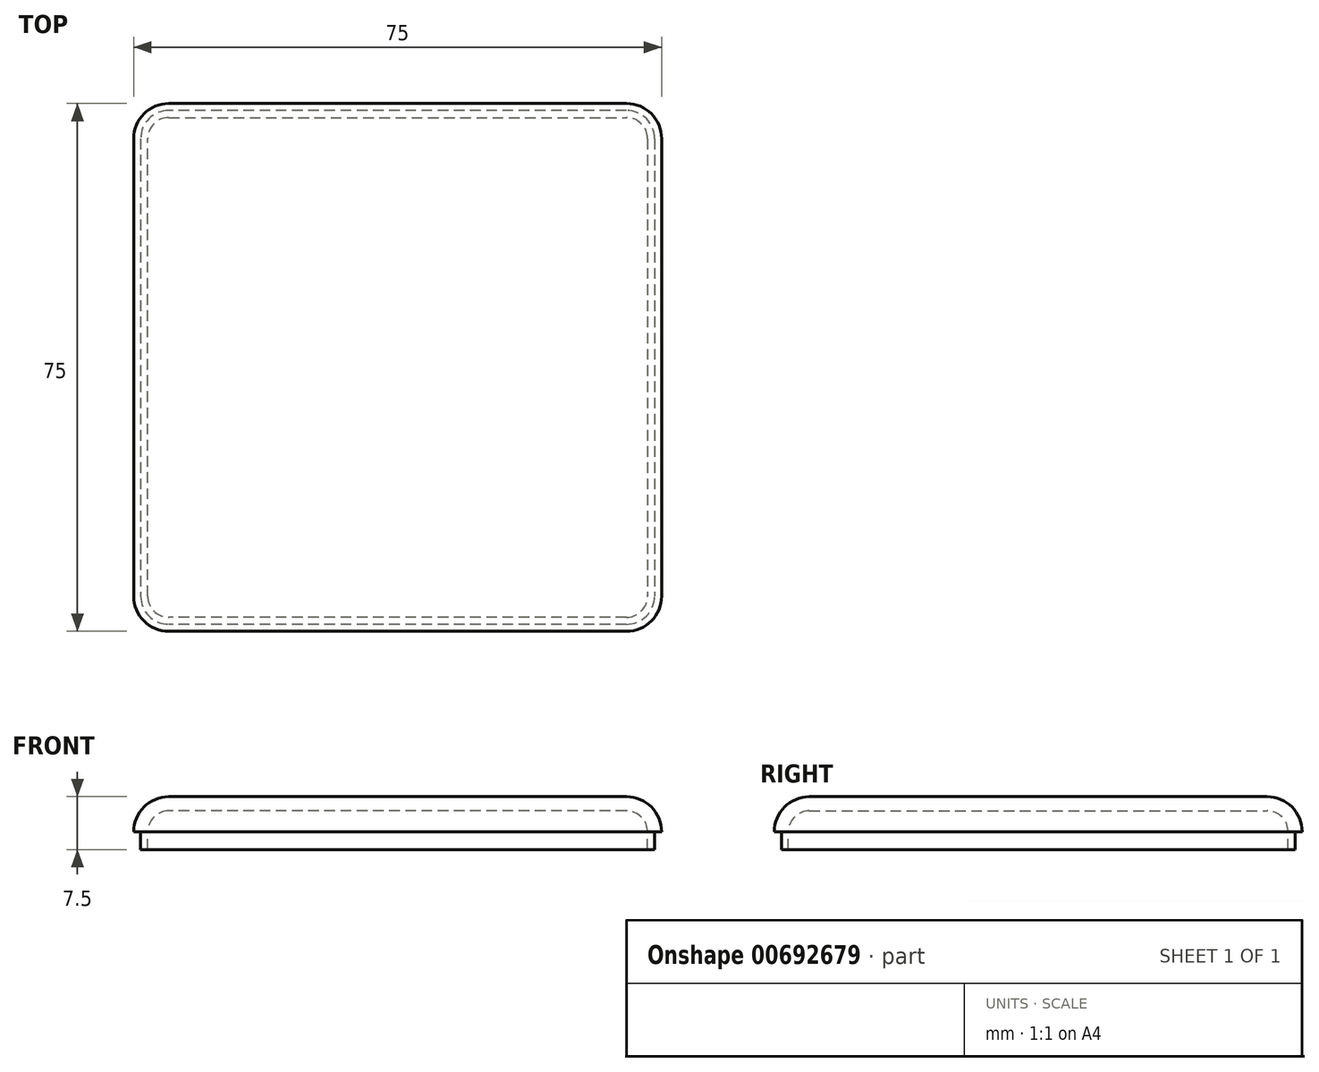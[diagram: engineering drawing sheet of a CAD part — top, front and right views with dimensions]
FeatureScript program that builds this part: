
annotation { "Feature Type Name" : "Feature", "Feature Type Description" : "" }
export const myFeature = defineFeature(function(context is Context, id is Id, definition is map)
    precondition{}
    {
        {
            var Q0;
            Q0=qCreatedBy(makeId("Top.planeOp"),FACE);
            var sketch = newSketch(context, id + "F0", { "sketchPlane" : qUnion([Q0])});
            skLineSegment(sketch, "E0.bottom", {"start": v(-37.5, 37.5) * mm, "end": v(37.5, 37.5) * mm});
            skLineSegment(sketch, "E0.top", {"start": v(-37.5, -37.5) * mm, "end": v(37.5, -37.5) * mm});
            skLineSegment(sketch, "E0.left", {"start": v(-37.5, 37.5) * mm, "end": v(-37.5, -37.5) * mm});
            skLineSegment(sketch, "E0.right", {"start": v(37.5, 37.5) * mm, "end": v(37.5, -37.5) * mm});
            skPoint(sketch, "E0.middle", {"position": v(0, 0) * mm});
            skLineSegment(sketch, "E1.0", {"start": v(-35.5, 35.5) * mm, "end": v(35.5, 35.5) * mm});
            skLineSegment(sketch, "E1.1", {"start": v(-35.5, 35.5) * mm, "end": v(-35.5, -35.5) * mm});
            skLineSegment(sketch, "E1.2", {"start": v(-35.5, -35.5) * mm, "end": v(35.5, -35.5) * mm});
            skLineSegment(sketch, "E1.3", {"start": v(35.5, 35.5) * mm, "end": v(35.5, -35.5) * mm});
            skSolve(sketch);
        }
        {
            var Q0;
            Q0=makeQuery(id+"F0.imprint","IMPRINT",FACE,{"disambiguationData":[TD([[makeQuery(id+"F0.imprint","IMPRINT",EDGE,{"derivedFrom":sQuery(id+"F0.wireOp",EDGE,"E1.0")}),-1.0]])]});
            var Q1;
            Q1=makeQuery(id+"F0.imprint","IMPRINT",FACE,{"disambiguationData":[TD([[makeQuery(id+"F0.imprint","IMPRINT",EDGE,{"derivedFrom":sQuery(id+"F0.wireOp",EDGE,"E0.bottom")}),-1.0]])]});
            extrude(context, id + "F1", {"entities" : qUnion([Q0, Q1]), "depth" : 5 * mm, "offsetDistance" : 25 * mm});
        }
        {
            var Q0;
            Q0=makeQuery(id+"F1.opExtrude","SWEPT_EDGE",EDGE,{"disambiguationData":[OSD([sQuery(id+"F0.wireOp",EDGE,"E0.top"),sQuery(id+"F0.wireOp",EDGE,"E0.left")])]});
            var Q1;
            Q1=makeQuery(id+"F1.opExtrude","SWEPT_EDGE",EDGE,{"disambiguationData":[OSD([sQuery(id+"F0.wireOp",EDGE,"E0.top"),sQuery(id+"F0.wireOp",EDGE,"E0.right")])]});
            var Q2;
            Q2=makeQuery(id+"F1.opExtrude","CAP_EDGE",EDGE,{"disambiguationData":[OSD([sQuery(id+"F0.wireOp",EDGE,"E0.top")])],"isStart":true});
            var Q3;
            Q3=makeQuery(id+"F1.opExtrude","CAP_EDGE",EDGE,{"disambiguationData":[OSD([sQuery(id+"F0.wireOp",EDGE,"E0.left")])],"isStart":true});
            var Q4;
            Q4=makeQuery(id+"F1.opExtrude","SWEPT_EDGE",EDGE,{"disambiguationData":[OSD([sQuery(id+"F0.wireOp",EDGE,"E0.bottom"),sQuery(id+"F0.wireOp",EDGE,"E0.left")])]});
            var Q5;
            Q5=makeQuery(id+"F1.opExtrude","CAP_EDGE",EDGE,{"disambiguationData":[OSD([sQuery(id+"F0.wireOp",EDGE,"E0.bottom")])],"isStart":true});
            var Q6;
            Q6=makeQuery(id+"F1.opExtrude","SWEPT_EDGE",EDGE,{"disambiguationData":[OSD([sQuery(id+"F0.wireOp",EDGE,"E0.bottom"),sQuery(id+"F0.wireOp",EDGE,"E0.right")])]});
            var Q7;
            Q7=makeQuery(id+"F1.opExtrude","CAP_EDGE",EDGE,{"disambiguationData":[OSD([sQuery(id+"F0.wireOp",EDGE,"E0.right")])],"isStart":true});
            fillet(context, id + "F2", {"entities" : qUnion([Q0, Q1, Q2, Q3, Q4, Q5, Q6, Q7]), "radius" : 5 * mm, "tangentPropagation" : true, "allowEdgeOverflow" : false});
        }
        {
            var Q0;
            Q0=makeQuery(id+"F1.opExtrude","CAP_FACE",FACE,{"disambiguationData":[OSD([sQuery(id+"F0.wireOp",EDGE,"E0.bottom"),sQuery(id+"F0.wireOp",EDGE,"E0.top"),sQuery(id+"F0.wireOp",EDGE,"E0.left"),sQuery(id+"F0.wireOp",EDGE,"E0.right")])],"isStart":false});
            shell(context, id + "F3", {"entities" : qUnion([Q0]), "thickness" : 2 * mm});
        }
        {
            var Q0;
            Q0=makeQuery(id+"F1.opExtrude","CAP_FACE",FACE,{"disambiguationData":[OSD([sQuery(id+"F0.wireOp",EDGE,"E0.bottom"),sQuery(id+"F0.wireOp",EDGE,"E0.top"),sQuery(id+"F0.wireOp",EDGE,"E0.left"),sQuery(id+"F0.wireOp",EDGE,"E0.right")])],"isStart":false});
            cPlane(context, id + "F4", {"entities" : qUnion([Q0]), "cplaneType" : CPlaneType.OFFSET, "offset" : 0 * mm, "width" : 150 * mm, "height" : 150 * mm});
        }
        {
            var Q0;
            Q0=qCreatedBy(id+"F4.planeOp",FACE);
            var sketch = newSketch(context, id + "F5", { "sketchPlane" : qUnion([Q0])});
            skArc(sketch, "E2.0", {"start": v(-36.5, -32.5) * mm, "mid": v(-35.33, -35.33) * mm, "end": v(-32.5, -36.5) * mm});
            skLineSegment(sketch, "E2.1", {"start": v(-36.5, 32.5) * mm, "end": v(-36.5, -32.5) * mm});
            skLineSegment(sketch, "E2.2", {"start": v(-32.5, -36.5) * mm, "end": v(32.5, -36.5) * mm});
            skArc(sketch, "E2.3", {"start": v(-32.5, 36.5) * mm, "mid": v(-35.33, 35.33) * mm, "end": v(-36.5, 32.5) * mm});
            skArc(sketch, "E2.4", {"start": v(32.5, -36.5) * mm, "mid": v(35.33, -35.33) * mm, "end": v(36.5, -32.5) * mm});
            skLineSegment(sketch, "E2.5", {"start": v(36.5, 32.5) * mm, "end": v(36.5, -32.5) * mm});
            skArc(sketch, "E2.6", {"start": v(36.5, 32.5) * mm, "mid": v(35.33, 35.33) * mm, "end": v(32.5, 36.5) * mm});
            skLineSegment(sketch, "E2.7", {"start": v(-32.5, 36.5) * mm, "end": v(32.5, 36.5) * mm});
            skLineSegment(sketch, "E3.0", {"start": v(-32.5, 35.5) * mm, "end": v(32.5, 35.5) * mm});
            skArc(sketch, "E4.0", {"start": v(35.5, 32.5) * mm, "mid": v(34.62, 34.62) * mm, "end": v(32.5, 35.5) * mm});
            skLineSegment(sketch, "E5.0", {"start": v(35.5, 32.5) * mm, "end": v(35.5, -32.5) * mm});
            skArc(sketch, "E6.0", {"start": v(32.5, -35.5) * mm, "mid": v(34.62, -34.62) * mm, "end": v(35.5, -32.5) * mm});
            skLineSegment(sketch, "E7.0", {"start": v(-32.5, -35.5) * mm, "end": v(32.5, -35.5) * mm});
            skArc(sketch, "E8.0", {"start": v(-35.5, -32.5) * mm, "mid": v(-34.62, -34.62) * mm, "end": v(-32.5, -35.5) * mm});
            skLineSegment(sketch, "E9.0", {"start": v(-35.5, 32.5) * mm, "end": v(-35.5, -32.5) * mm});
            skArc(sketch, "E10.0", {"start": v(-32.5, 35.5) * mm, "mid": v(-34.62, 34.62) * mm, "end": v(-35.5, 32.5) * mm});
            skSolve(sketch);
        }
        {
            var Q0;
            Q0=makeQuery(id+"F5.imprint","IMPRINT",FACE,{"disambiguationData":[TD([[makeQuery(id+"F5.imprint","IMPRINT",EDGE,{"derivedFrom":sQuery(id+"F5.wireOp",EDGE,"E2.0")}),1.0]])]});
            extrude(context, id + "F6", {"entities" : qUnion([Q0]), "operationType" : NewBodyOperationType.ADD, "depth" : 2.5 * mm, "offsetDistance" : 25 * mm});
        }
        {
            var Q0;
            Q0=qCreatedBy(makeId("Top.planeOp"),FACE);
            var sketch = newSketch(context, id + "F7", { "sketchPlane" : qUnion([Q0])});
            skLineSegment(sketch, "E11", {"start": v(0, -41.9) * mm, "end": v(0, 56.18) * mm, "construction": true});
            skSolve(sketch);
        }
        {
            var Q0;
            Q0=makeQuery(id+"F1.opExtrude","SWEPT_BODY",BODY,{"disambiguationData":[OSD([sQuery(id+"F0.wireOp",EDGE,"E0.bottom"),sQuery(id+"F0.wireOp",EDGE,"E0.top"),sQuery(id+"F0.wireOp",EDGE,"E0.left"),sQuery(id+"F0.wireOp",EDGE,"E0.right")])]});
            var Q1;
            Q1=sQuery(id+"F7.wireOp",EDGE,"E11");
            transform(context, id + "F8", {"entities" : qUnion([Q0]), "transformType" : TransformType.ROTATION, "transformAxis" : qUnion([Q1]), "angle" : 180 * degree, "makeCopy" : false});
        }
        {
            var Q0;
            Q0=makeQuery(id+"F1.opExtrude","SWEPT_BODY",BODY,{"disambiguationData":[OSD([sQuery(id+"F0.wireOp",EDGE,"E0.bottom"),sQuery(id+"F0.wireOp",EDGE,"E0.top"),sQuery(id+"F0.wireOp",EDGE,"E0.left"),sQuery(id+"F0.wireOp",EDGE,"E0.right")])]});
            transform(context, id + "F9", {"entities" : qUnion([Q0]), "transformType" : TransformType.TRANSLATION_3D, "dx" : 0 * mm, "dy" : 0 * mm, "dz" : 7.5 * mm, "makeCopy" : false});
        }
    });
